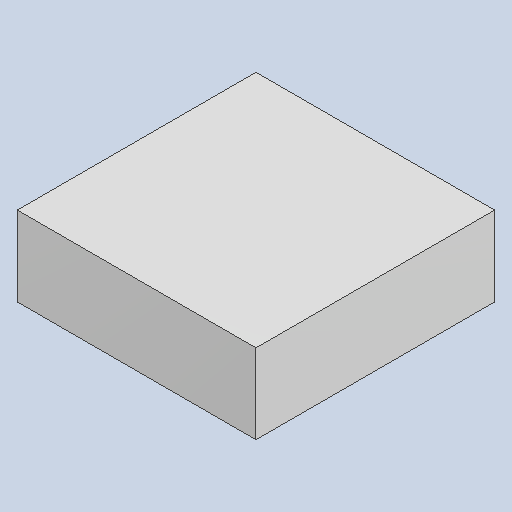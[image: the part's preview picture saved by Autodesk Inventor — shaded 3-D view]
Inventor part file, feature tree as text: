
AUTODESK INVENTOR PART (.ipt)
format: ipt  version: 2023.4 (Build 274418000, 418)  size: 79,872 bytes
history: native  units: mm
features: extrude x1
ambient origin geometry x8: Origin, YZ Plane, XZ Plane, XY Plane, X Axis, Y Axis, Z Axis, Center Point
bodies: Solid1 (feature_tree)
feature tree (1):
  extrude  "Extruded_57"  [1 undecoded]
note: 1 required parameter value undecoded (feature->parameter linkage not recoverable at this tier; creation-order binding heuristic only, values carry confidence <= 0.55)
